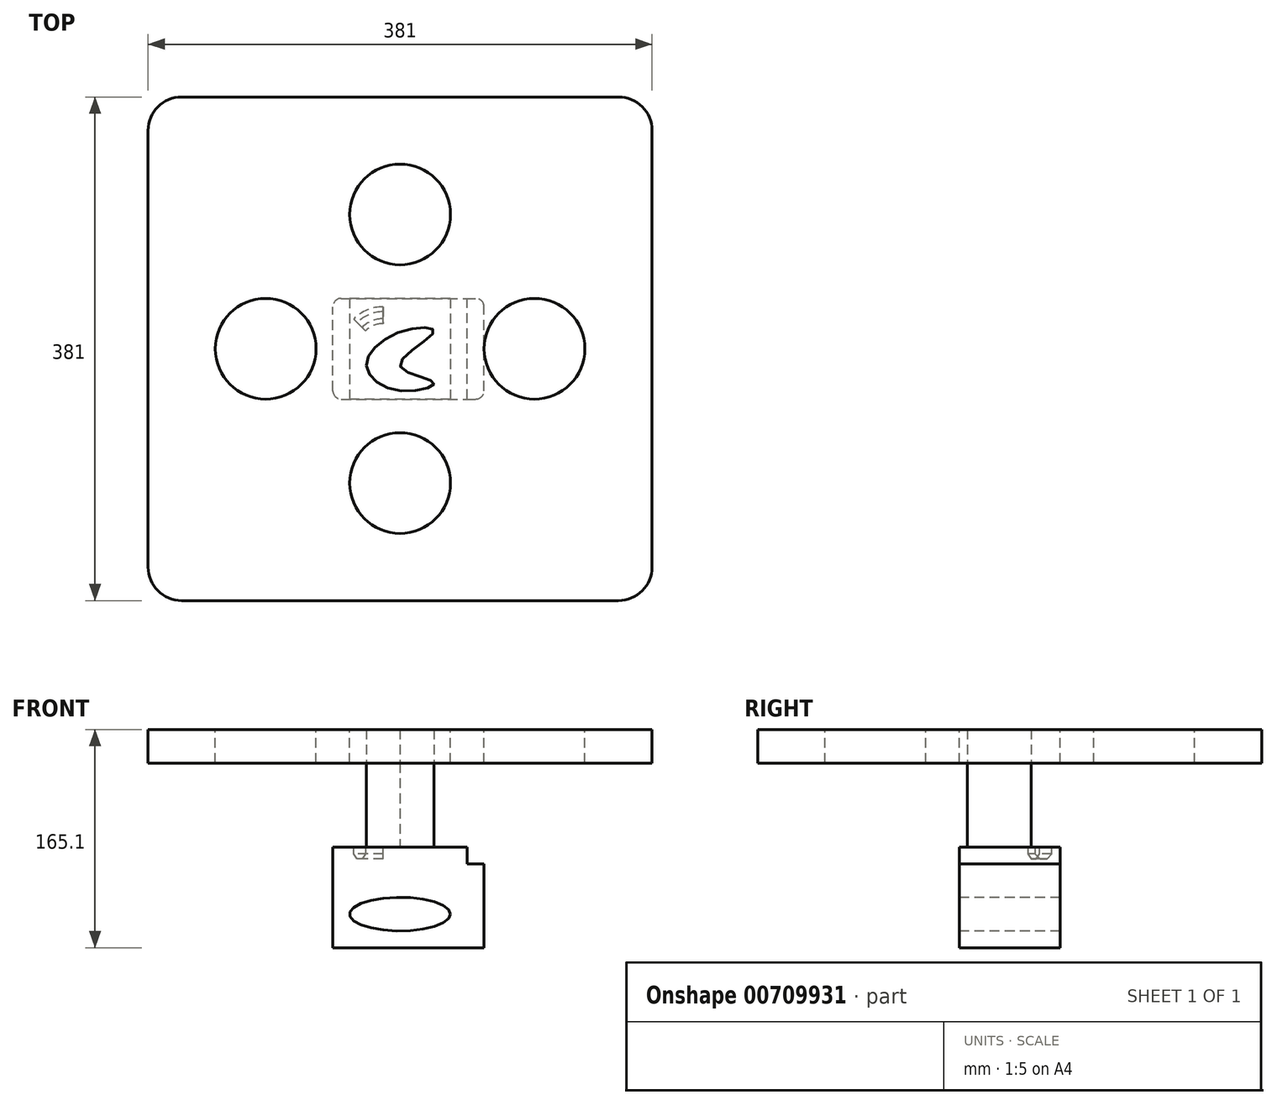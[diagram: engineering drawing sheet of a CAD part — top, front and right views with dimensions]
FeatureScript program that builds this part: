
annotation { "Feature Type Name" : "Feature", "Feature Type Description" : "" }
export const myFeature = defineFeature(function(context is Context, id is Id, definition is map)
    precondition{}
    {
        {
            var Q0;
            Q0=qCreatedBy(makeId("Front.planeOp"),FACE);
            var sketch = newSketch(context, id + "F0", { "sketchPlane" : qUnion([Q0])});
            skLineSegment(sketch, "E0.bottom", {"start": v(0, 0) * mm, "end": v(101.6, 0) * mm});
            skLineSegment(sketch, "E0.top", {"start": v(0, 76.2) * mm, "end": v(101.6, 76.2) * mm});
            skLineSegment(sketch, "E0.left", {"start": v(0, 0) * mm, "end": v(0, 76.2) * mm});
            skLineSegment(sketch, "E0.right", {"start": v(101.6, 63.5) * mm, "end": v(101.6, 76.2) * mm});
            skLineSegment(sketch, "E1.bottom", {"start": v(101.6, 63.5) * mm, "end": v(114.3, 63.5) * mm});
            skLineSegment(sketch, "E1.top", {"start": v(88.83, 0) * mm, "end": v(114.3, 0) * mm});
            skLineSegment(sketch, "E1.right", {"start": v(114.3, 63.5) * mm, "end": v(114.3, 0) * mm});
            skSolve(sketch);
        }
        {
            var Q0;
            {var subQ0=sQuery(id+"F0.wireOp",EDGE,"E0.bottom");Q0=makeQuery(id+"F0.imprint","IMPRINT",FACE,{"disambiguationData":[TD([[makeQuery(id+"F0.imprint","IMPRINT",EDGE,{"derivedFrom":subQ0}),1.0]])]});}
            extrude(context, id + "F1", {"entities" : qUnion([Q0]), "depth" : 76.2 * mm, "offsetDistance" : 25.4 * mm});
        }
        {
            var Q0;
            Q0=makeQuery(id+"F1.opExtrude","CAP_FACE",FACE,{"disambiguationData":[OSD([sQuery(id+"F0.wireOp",EDGE,"E0.bottom"),sQuery(id+"F0.wireOp",EDGE,"E0.top"),sQuery(id+"F0.wireOp",EDGE,"E0.left"),sQuery(id+"F0.wireOp",EDGE,"E0.right"),sQuery(id+"F0.wireOp",EDGE,"E1.bottom"),sQuery(id+"F0.wireOp",EDGE,"E1.top"),sQuery(id+"F0.wireOp",EDGE,"E1.right")])],"isStart":false});
            var sketch = newSketch(context, id + "F2", { "sketchPlane" : qUnion([Q0])});
            skEllipse(sketch, "E2", {"center": v(50.8, 25.4) * mm, "majorRadius": 38.1 * mm, "minorRadius": 12.7 * mm, "majorAxis": v(1, 0)});
            skLineSegment(sketch, "E3", {"start": v(88.9, 25.4) * mm, "end": v(12.7, 25.4) * mm, "construction": true});
            skSolve(sketch);
        }
        {
            var Q0;
            Q0 = qSketchRegion(id + "F2", true);
            var Q1;
            Q1=makeQuery(id+"F1.opExtrude","CAP_FACE",FACE,{"disambiguationData":[OSD([sQuery(id+"F0.wireOp",EDGE,"E0.bottom"),sQuery(id+"F0.wireOp",EDGE,"E0.top"),sQuery(id+"F0.wireOp",EDGE,"E0.left"),sQuery(id+"F0.wireOp",EDGE,"E0.right"),sQuery(id+"F0.wireOp",EDGE,"E1.bottom"),sQuery(id+"F0.wireOp",EDGE,"E1.top"),sQuery(id+"F0.wireOp",EDGE,"E1.right")])],"isStart":true});
            extrude(context, id + "F3", {"entities" : qUnion([Q0]), "operationType" : NewBodyOperationType.REMOVE, "endBound" : BoundingType.UP_TO_SURFACE, "oppositeDirection" : true, "depth" : 25.4 * mm, "endBoundEntityFace" : qUnion([Q1]), "offsetDistance" : 25.4 * mm});
        }
        {
            var Q0;
            Q0=makeQuery(id+"F1.opExtrude","CAP_FACE",FACE,{"disambiguationData":[OSD([sQuery(id+"F0.wireOp",EDGE,"E0.bottom"),sQuery(id+"F0.wireOp",EDGE,"E0.top"),sQuery(id+"F0.wireOp",EDGE,"E0.left"),sQuery(id+"F0.wireOp",EDGE,"E0.right"),sQuery(id+"F0.wireOp",EDGE,"E1.bottom"),sQuery(id+"F0.wireOp",EDGE,"E1.top"),sQuery(id+"F0.wireOp",EDGE,"E1.right")])],"isStart":false});
            cPlane(context, id + "F4", {"entities" : qUnion([Q0]), "cplaneType" : CPlaneType.OFFSET, "offset" : 38.1 * mm, "oppositeDirection" : true, "width" : 152.4 * mm, "height" : 152.4 * mm});
        }
        {
            var Q0;
            Q0=qCreatedBy(id+"F4.planeOp",FACE);
            var sketch = newSketch(context, id + "F5", { "sketchPlane" : qUnion([Q0])});
            skCircle(sketch, "E4.cCircle", {"center": v(12.7, 73.57) * mm, "radius": 6.35 * mm, "construction": true});
            skLineSegment(sketch, "E4.0", {"start": v(6.35, 70.94) * mm, "end": v(6.35, 76.2) * mm});
            skLineSegment(sketch, "E4.1", {"start": v(6.35, 76.2) * mm, "end": v(10.07, 79.92) * mm});
            skLineSegment(sketch, "E4.2", {"start": v(10.07, 79.92) * mm, "end": v(15.33, 79.92) * mm});
            skLineSegment(sketch, "E4.3", {"start": v(15.33, 79.92) * mm, "end": v(19.05, 76.2) * mm});
            skLineSegment(sketch, "E4.4", {"start": v(19.05, 76.2) * mm, "end": v(19.05, 70.94) * mm});
            skLineSegment(sketch, "E4.5", {"start": v(19.05, 70.94) * mm, "end": v(15.33, 67.22) * mm});
            skLineSegment(sketch, "E4.6", {"start": v(15.33, 67.22) * mm, "end": v(10.07, 67.22) * mm});
            skLineSegment(sketch, "E4.7", {"start": v(10.07, 67.22) * mm, "end": v(6.35, 70.94) * mm});
            skLineSegment(sketch, "E5", {"start": v(38.1, 76.2) * mm, "end": v(38.1, 0) * mm});
            skLineSegment(sketch, "E6", {"start": v(38.1, 0) * mm, "end": v(38.1, 76.2) * mm});
            skSolve(sketch);
        }
        {
            var Q0;
            Q0 = qSketchRegion(id + "F5", true);
            var Q1;
            Q1=sQuery(id+"F5.wireOp",EDGE,"E5");
            revolve(context, id + "F6", {"operationType" : NewBodyOperationType.REMOVE, "surfaceOperationType" : NewSurfaceOperationType.NEW, "entities" : qUnion([Q0]), "axis" : qUnion([Q1]), "revolveType" : RevolveType.TWO_DIRECTIONS, "angle" : 90 * degree, "angleBack" : 45 * degree});
        }
        {
            var Q0;
            Q0=makeQuery(id+"F1.opExtrude","SWEPT_FACE",FACE,{"disambiguationData":[OSD([sQuery(id+"F0.wireOp",EDGE,"E0.top")])]});
            var sketch = newSketch(context, id + "F7", { "sketchPlane" : qUnion([Q0])});
            skFitSpline(sketch, "E7", {"points": [v(25.4, -50.8) * mm, v(50.8, -69.85) * mm, v(76.2, -63.5) * mm, v(50.8, -50.8) * mm, v(76.2, -25.4) * mm, v(50.8, -25.4) * mm, v(25.4, -50.8) * mm]});
            skSolve(sketch);
        }
        {
            var Q0;
            Q0 = qSketchRegion(id + "F7", true);
            extrude(context, id + "F8", {"entities" : qUnion([Q0]), "operationType" : NewBodyOperationType.ADD, "depth" : 63.5 * mm, "offsetDistance" : 25.4 * mm});
        }
        {
            var Q0;
            Q0=makeQuery(id+"F1.opExtrude","CAP_EDGE",EDGE,{"disambiguationData":[OSD([sQuery(id+"F0.wireOp",EDGE,"E0.left")])],"isStart":false});
            var Q1;
            Q1=makeQuery(id+"F1.opExtrude","CAP_EDGE",EDGE,{"disambiguationData":[OSD([sQuery(id+"F0.wireOp",EDGE,"E0.left")])],"isStart":true});
            var Q2;
            Q2=makeQuery(id+"F1.opExtrude","CAP_EDGE",EDGE,{"disambiguationData":[OSD([sQuery(id+"F0.wireOp",EDGE,"E1.right")])],"isStart":false});
            var Q3;
            Q3=makeQuery(id+"F1.opExtrude","CAP_EDGE",EDGE,{"disambiguationData":[OSD([sQuery(id+"F0.wireOp",EDGE,"E1.right")])],"isStart":true});
            fillet(context, id + "F9", {"entities" : qUnion([Q0, Q1, Q2, Q3]), "radius" : 6.35 * mm, "tangentPropagation" : true, "allowEdgeOverflow" : false});
        }
        {
            var Q0;
            Q0=makeQuery(id+"F8.opExtrude","CAP_FACE",FACE,{"disambiguationData":[OSD([sQuery(id+"F7.wireOp",EDGE,"E7")])],"isStart":false});
            var sketch = newSketch(context, id + "F10", { "sketchPlane" : qUnion([Q0])});
            skLineSegment(sketch, "E8.bottom", {"start": v(-114.3, 152.4) * mm, "end": v(215.9, 152.4) * mm});
            skLineSegment(sketch, "E8.top", {"start": v(-114.3, -228.6) * mm, "end": v(215.9, -228.6) * mm});
            skLineSegment(sketch, "E8.left", {"start": v(-139.7, 127) * mm, "end": v(-139.7, -203.2) * mm});
            skLineSegment(sketch, "E8.right", {"start": v(241.3, 127) * mm, "end": v(241.3, -203.2) * mm});
            skPoint(sketch, "E9.visualSharp", {"position": v(241.3, -228.6) * mm});
            skArc(sketch, "E9.filletArc", {"start": v(215.9, -228.6) * mm, "mid": v(233.86, -221.16) * mm, "end": v(241.3, -203.2) * mm});
            skPoint(sketch, "E10.visualSharp", {"position": v(-139.7, -228.6) * mm});
            skArc(sketch, "E10.filletArc", {"start": v(-139.7, -203.2) * mm, "mid": v(-132.26, -221.16) * mm, "end": v(-114.3, -228.6) * mm});
            skPoint(sketch, "E11.visualSharp", {"position": v(241.3, 152.4) * mm});
            skArc(sketch, "E11.filletArc", {"start": v(241.3, 127) * mm, "mid": v(233.86, 144.96) * mm, "end": v(215.9, 152.4) * mm});
            skPoint(sketch, "E12.visualSharp", {"position": v(-139.7, 152.4) * mm});
            skArc(sketch, "E12.filletArc", {"start": v(-114.3, 152.4) * mm, "mid": v(-132.26, 144.96) * mm, "end": v(-139.7, 127) * mm});
            skSolve(sketch);
        }
        {
            var Q0;
            Q0=makeQuery(id+"F10.imprint","IMPRINT",FACE,{"disambiguationData":[TD([[makeQuery(id+"F10.imprint","IMPRINT",EDGE,{"derivedFrom":sQuery(id+"F10.wireOp",EDGE,"E8.bottom")}),-1.0]])]});
            extrude(context, id + "F11", {"entities" : qUnion([Q0]), "depth" : 25.4 * mm, "offsetDistance" : 25.4 * mm});
        }
        {
            var Q0;
            Q0=makeQuery(id+"F11.opExtrude","CAP_FACE",FACE,{"disambiguationData":[OSD([sQuery(id+"F7.wireOp",EDGE,"E7"),sQuery(id+"F10.wireOp",EDGE,"E8.bottom"),sQuery(id+"F10.wireOp",EDGE,"E8.top"),sQuery(id+"F10.wireOp",EDGE,"E8.left"),sQuery(id+"F10.wireOp",EDGE,"E8.right"),sQuery(id+"F10.wireOp",EDGE,"E9.filletArc"),sQuery(id+"F10.wireOp",EDGE,"E10.filletArc"),sQuery(id+"F10.wireOp",EDGE,"E11.filletArc"),sQuery(id+"F10.wireOp",EDGE,"E12.filletArc")])],"isStart":false});
            var sketch = newSketch(context, id + "F12", { "sketchPlane" : qUnion([Q0])});
            skLineSegment(sketch, "E13", {"start": v(50.8, 152.4) * mm, "end": v(50.8, -228.6) * mm, "construction": true});
            skLineSegment(sketch, "E14", {"start": v(241.3, -38.1) * mm, "end": v(-139.7, -38.1) * mm, "construction": true});
            skPoint(sketch, "E15", {"position": v(50.8, -38.1) * mm});
            skCircle(sketch, "E16", {"center": v(-50.8, -38.1) * mm, "radius": 38.1 * mm});
            skCircle(sketch, "E17.1.0", {"center": v(50.8, 63.5) * mm, "radius": 38.1 * mm});
            skCircle(sketch, "E17.2.0", {"center": v(152.4, -38.1) * mm, "radius": 38.1 * mm});
            skLineSegment(sketch, "E17.anchor1", {"start": v(50.8, -38.1) * mm, "end": v(-50.8, -38.1) * mm, "construction": true});
            skLineSegment(sketch, "E17.anchor2", {"start": v(50.8, -38.1) * mm, "end": v(50.8, -139.7) * mm, "construction": true});
            skCircle(sketch, "E18.1.3.0", {"center": v(50.8, -139.7) * mm, "radius": 38.1 * mm});
            skSolve(sketch);
        }
        {
            var Q0;
            Q0=makeQuery(id+"F12.imprint","IMPRINT",FACE,{"disambiguationData":[TD([[makeQuery(id+"F12.imprint","IMPRINT",EDGE,{"derivedFrom":sQuery(id+"F12.wireOp",EDGE,"E16")}),1.0]])]});
            var Q1;
            Q1=makeQuery(id+"F12.imprint","IMPRINT",FACE,{"disambiguationData":[TD([[makeQuery(id+"F12.imprint","IMPRINT",EDGE,{"derivedFrom":sQuery(id+"F12.wireOp",EDGE,"E18.1.3.0")}),1.0]])]});
            var Q2;
            Q2=makeQuery(id+"F12.imprint","IMPRINT",FACE,{"disambiguationData":[TD([[makeQuery(id+"F12.imprint","IMPRINT",EDGE,{"derivedFrom":sQuery(id+"F12.wireOp",EDGE,"E17.2.0")}),1.0]])]});
            var Q3;
            Q3=makeQuery(id+"F12.imprint","IMPRINT",FACE,{"disambiguationData":[TD([[makeQuery(id+"F12.imprint","IMPRINT",EDGE,{"derivedFrom":sQuery(id+"F12.wireOp",EDGE,"E17.1.0")}),1.0]])]});
            var Q4;
            Q4=sQuery(id+"F12.wireOp",EDGE,"E16");
            var Q5;
            Q5=makeQuery(id+"F11.opExtrude","CAP_FACE",FACE,{"disambiguationData":[OSD([sQuery(id+"F7.wireOp",EDGE,"E7"),sQuery(id+"F10.wireOp",EDGE,"E8.bottom"),sQuery(id+"F10.wireOp",EDGE,"E8.top"),sQuery(id+"F10.wireOp",EDGE,"E8.left"),sQuery(id+"F10.wireOp",EDGE,"E8.right"),sQuery(id+"F10.wireOp",EDGE,"E9.filletArc"),sQuery(id+"F10.wireOp",EDGE,"E10.filletArc"),sQuery(id+"F10.wireOp",EDGE,"E11.filletArc"),sQuery(id+"F10.wireOp",EDGE,"E12.filletArc")])],"isStart":true});
            extrude(context, id + "F13", {"entities" : qUnion([Q0, Q1, Q2, Q3]), "operationType" : NewBodyOperationType.REMOVE, "surfaceEntities" : qUnion([Q4]), "endBound" : BoundingType.UP_TO_SURFACE, "oppositeDirection" : true, "depth" : 25.4 * mm, "endBoundEntityFace" : qUnion([Q5]), "offsetDistance" : 25.4 * mm});
        }
    });
